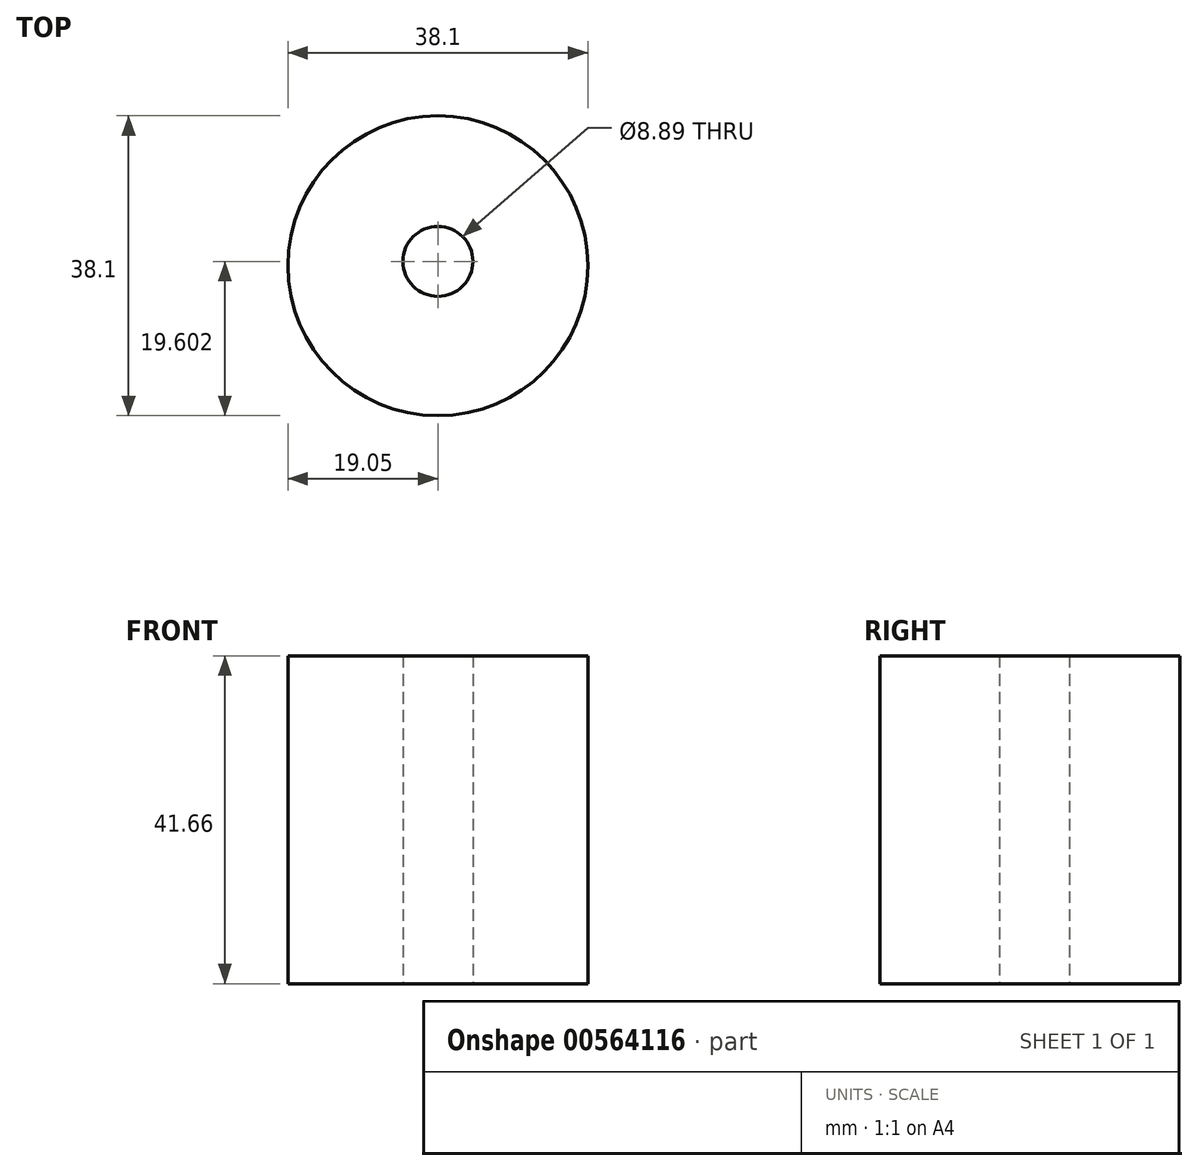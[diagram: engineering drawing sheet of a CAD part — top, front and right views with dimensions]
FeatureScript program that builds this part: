
annotation { "Feature Type Name" : "Feature", "Feature Type Description" : "" }
export const myFeature = defineFeature(function(context is Context, id is Id, definition is map)
    precondition{}
    {
        {
            var Q0;
            Q0=qCreatedBy(makeId("Top.planeOp"),FACE);
            var sketch = newSketch(context, id + "F0", { "sketchPlane" : qUnion([Q0])});
            skCircle(sketch, "E0", {"center": v(0, 0) * mm, "radius": 19.05 * mm});
            skCircle(sketch, "E1", {"center": v(0, 0.55) * mm, "radius": 4.45 * mm});
            skSolve(sketch);
        }
        {
            var Q0;
            Q0=makeQuery(id+"F0.imprint","IMPRINT",FACE,{"disambiguationData":[TD([[makeQuery(id+"F0.imprint","IMPRINT",EDGE,{"derivedFrom":sQuery(id+"F0.wireOp",EDGE,"E0")}),1.0]])]});
            extrude(context, id + "F1", {"entities" : qUnion([Q0]), "depth" : 41.66 * mm, "offsetDistance" : 25.4 * mm});
        }
    });
